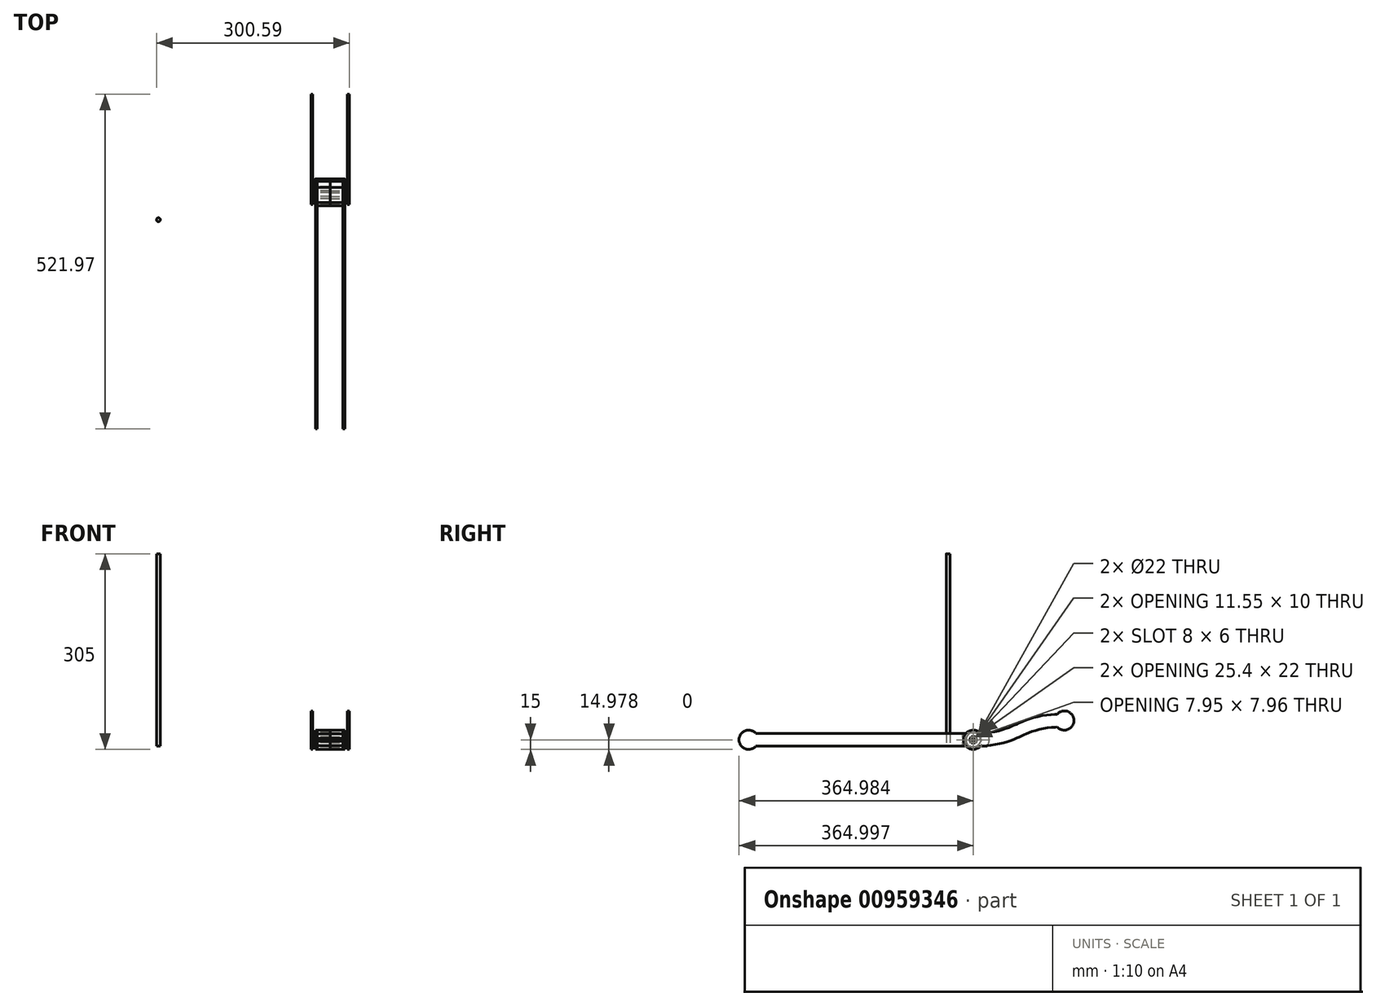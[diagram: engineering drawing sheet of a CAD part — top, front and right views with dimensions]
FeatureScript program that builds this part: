
annotation { "Feature Type Name" : "Feature", "Feature Type Description" : "" }
export const myFeature = defineFeature(function(context is Context, id is Id, definition is map)
    precondition{}
    {
        {
            var Q0;
            Q0=qCreatedBy(makeId("Right.planeOp"),FACE);
            var sketch = newSketch(context, id + "F0", { "sketchPlane" : qUnion([Q0])});
            skLineSegment(sketch, "E0", {"start": v(-170.3, 0) * mm, "end": v(157.34, 0) * mm});
            skLineSegment(sketch, "E1.0", {"start": v(-170.3, 20) * mm, "end": v(157.34, 20) * mm});
            skLineSegment(sketch, "E2.0", {"start": v(-181.48, 10) * mm, "end": v(168.52, 10) * mm, "construction": true});
            skArc(sketch, "E3", {"start": v(157.34, 0) * mm, "mid": v(168.52, -5) * mm, "end": v(179.7, 0) * mm});
            skArc(sketch, "E4", {"start": v(-170.3, 20) * mm, "mid": v(-196.48, 10) * mm, "end": v(-170.3, 0) * mm});
            skPoint(sketch, "E5.end.orphan", {"position": v(-181.48, 0) * mm});
            skLineSegment(sketch, "E6", {"start": v(179.7, 20) * mm, "end": v(189.7, 20) * mm});
            skLineSegment(sketch, "E7", {"start": v(179.7, 0) * mm, "end": v(189.7, 0) * mm});
            skArc(sketch, "E8", {"start": v(189.7, 0) * mm, "mid": v(193.52, 10) * mm, "end": v(189.7, 20) * mm});
            skArc(sketch, "E9.trimOffspring", {"start": v(179.7, 20) * mm, "mid": v(168.52, 25) * mm, "end": v(157.34, 20) * mm});
            skSolve(sketch);
        }
        {
            var Q0;
            Q0=qCreatedBy(makeId("Right.planeOp"),FACE);
            cPlane(context, id + "F1", {"entities" : qUnion([Q0]), "cplaneType" : CPlaneType.OFFSET, "offset" : 20 * mm, "width" : 150 * mm, "height" : 150 * mm});
        }
        {
            var Q0;
            Q0=qCreatedBy(id+"F1.planeOp",FACE);
            var sketch = newSketch(context, id + "F2", { "sketchPlane" : qUnion([Q0])});
            skLineSegment(sketch, "E10.0.0", {"start": v(-170.3, 0) * mm, "end": v(157.34, 0) * mm});
            skLineSegment(sketch, "E10.0.1", {"start": v(157.34, 0) * mm, "end": v(157.34, 0) * mm});
            skLineSegment(sketch, "E10.0.2", {"start": v(157.34, 20) * mm, "end": v(-170.3, 20) * mm});
            skArc(sketch, "E10.0.3", {"start": v(-170.3, 20) * mm, "mid": v(-196.48, 10) * mm, "end": v(-170.3, 0) * mm});
            skPoint(sketch, "E11.0", {"position": v(168.52, 25) * mm});
            skArc(sketch, "E12.0", {"start": v(179.7, 20) * mm, "mid": v(168.52, 25) * mm, "end": v(157.34, 20) * mm});
            skArc(sketch, "E13.0", {"start": v(157.34, 0) * mm, "mid": v(168.52, -5) * mm, "end": v(179.7, 0) * mm});
            skLineSegment(sketch, "E14.0", {"start": v(179.7, 0) * mm, "end": v(189.7, 0) * mm});
            skArc(sketch, "E15.0", {"start": v(189.7, 0) * mm, "mid": v(193.52, 10) * mm, "end": v(189.7, 20) * mm});
            skPoint(sketch, "E16.0", {"position": v(184.7, 20) * mm});
            skLineSegment(sketch, "E17.0", {"start": v(179.7, 20) * mm, "end": v(189.7, 20) * mm});
            skSolve(sketch);
        }
        {
            var Q0;
            Q0=qCreatedBy(makeId("Right.planeOp"),FACE);
            var sketch = newSketch(context, id + "F3", { "sketchPlane" : qUnion([Q0])});
            skArc(sketch, "E18.converted", {"start": v(179.48, 20.24) * mm, "mid": v(153.52, 9.68) * mm, "end": v(179.9, 0.24) * mm});
            skPoint(sketch, "E19.orphan", {"position": v(179.7, 0) * mm});
            skCircle(sketch, "E20", {"center": v(310.5, 40) * mm, "radius": 100 * mm, "construction": true});
            skLineSegment(sketch, "E21", {"start": v(-192.7, -60) * mm, "end": v(245.23, -60) * mm, "construction": true});
            skArc(sketch, "E22", {"start": v(295.5, 40) * mm, "mid": v(295.5, 39.78) * mm, "end": v(295.5, 39.55) * mm});
            skFitSpline(sketch, "E23", {"points": [v(168.52, 10) * mm, v(310.5, 40) * mm], "startDerivative": vector(225, 0) * mm, "endDerivative": vector(225, 0) * mm, "construction": true});
            skLineSegment(sketch, "E24", {"start": v(310.5, 40) * mm, "end": v(235.5, 40) * mm, "construction": true});
            skLineSegment(sketch, "E25", {"start": v(168.52, 10) * mm, "end": v(243.52, 10) * mm, "construction": true});
            skFitSpline(sketch, "E26.0", {"points": [v(168.52, 20) * mm, v(173.04, 20) * mm, v(181.4, 20.23) * mm, v(192.18, 21.14) * mm, v(201.44, 22.54) * mm, v(209.47, 24.32) * mm, v(216.56, 26.42) * mm, v(221.96, 28.38) * mm, v(226.13, 30.06) * mm, v(229.22, 31.37) * mm, v(232.3, 32.73) * mm, v(235.4, 34.12) * mm, v(238.58, 35.54) * mm, v(241.84, 36.98) * mm, v(245.21, 38.41) * mm, v(249.9, 40.3) * mm, v(256.18, 42.59) * mm, v(264.56, 45.06) * mm, v(273.96, 47.15) * mm, v(284.55, 48.74) * mm, v(296.55, 49.76) * mm, v(305.64, 50) * mm, v(310.5, 50) * mm]});
            skFitSpline(sketch, "E27.0", {"points": [v(168.52, 0) * mm, v(173.37, 0) * mm, v(182.46, 0.24) * mm, v(194.46, 1.26) * mm, v(205.05, 2.85) * mm, v(214.45, 4.94) * mm, v(222.83, 7.41) * mm, v(229.1, 9.7) * mm, v(233.8, 11.59) * mm, v(237.18, 13.02) * mm, v(240.43, 14.46) * mm, v(243.6, 15.88) * mm, v(246.71, 17.27) * mm, v(249.8, 18.63) * mm, v(252.88, 19.94) * mm, v(257.05, 21.62) * mm, v(262.45, 23.58) * mm, v(269.54, 25.68) * mm, v(277.57, 27.46) * mm, v(286.83, 28.86) * mm, v(297.6, 29.77) * mm, v(305.97, 30) * mm, v(310.5, 30) * mm]});
            skArc(sketch, "E28.trimOffspring", {"start": v(183.52, 10) * mm, "mid": v(183.52, 10.22) * mm, "end": v(183.51, 10.45) * mm});
            skArc(sketch, "E29.trimOffspring", {"start": v(299.53, 29.76) * mm, "mid": v(325.49, 40.32) * mm, "end": v(299.1, 49.76) * mm});
            skArc(sketch, "E30", {"start": v(310.5, 40) * mm, "mid": v(305.5, 57.9) * mm, "end": v(298.26, 75) * mm, "construction": true});
            skCircle(sketch, "E31", {"center": v(298.26, 75) * mm, "radius": 100 * mm, "construction": true});
            skSolve(sketch);
        }
        {
            var Q0;
            Q0=makeQuery(id+"F2.imprint","IMPRINT",FACE,{"disambiguationData":[TD([[makeQuery(id+"F2.imprint","IMPRINT",EDGE,{"derivedFrom":sQuery(id+"F2.wireOp",EDGE,"E10.0.0")}),1.0]])]});
            extrude(context, id + "F4", {"entities" : qUnion([Q0]), "depth" : 3 * mm, "offsetDistance" : 25 * mm});
        }
        {
            var Q0;
            Q0=makeQuery(id+"F2.imprint","IMPRINT",FACE,{"disambiguationData":[TD([[makeQuery(id+"F2.imprint","IMPRINT",EDGE,{"derivedFrom":sQuery(id+"F2.wireOp",EDGE,"E10.0.0")}),1.0]])]});
            var sketch = newSketch(context, id + "F5", { "sketchPlane" : qUnion([Q0])});
            skPoint(sketch, "E32.0", {"position": v(168.52, 10) * mm});
            skPoint(sketch, "E33.0.midPoint", {"position": v(161.02, 0) * mm});
            skArc(sketch, "E34.cCircle", {"start": v(180.82, 18.58) * mm, "mid": v(168.52, 25) * mm, "end": v(156.22, 18.58) * mm});
            skPoint(sketch, "E34.0.midPoint", {"position": v(181.5, 17.5) * mm});
            skCircle(sketch, "E35.cCircle", {"center": v(168.52, 10) * mm, "radius": 5 * mm, "construction": true});
            skLineSegment(sketch, "E35.0", {"start": v(171.4, 5) * mm, "end": v(165.63, 5) * mm});
            skLineSegment(sketch, "E35.1", {"start": v(165.63, 5) * mm, "end": v(162.74, 10) * mm});
            skLineSegment(sketch, "E35.2", {"start": v(162.74, 10) * mm, "end": v(165.63, 15) * mm});
            skLineSegment(sketch, "E35.3", {"start": v(165.63, 15) * mm, "end": v(171.4, 15) * mm});
            skLineSegment(sketch, "E35.4", {"start": v(171.4, 15) * mm, "end": v(174.3, 10) * mm});
            skLineSegment(sketch, "E35.5", {"start": v(174.3, 10) * mm, "end": v(171.4, 5) * mm});
            skPoint(sketch, "E35.0.midPoint", {"position": v(168.52, 5) * mm});
            skCircle(sketch, "E36.cCircle", {"center": v(168.52, 10) * mm, "radius": 11 * mm});
            skLineSegment(sketch, "E36.0", {"start": v(162.17, 21) * mm, "end": v(174.87, 21) * mm});
            skLineSegment(sketch, "E36.1", {"start": v(174.87, 21) * mm, "end": v(181.22, 10) * mm});
            skLineSegment(sketch, "E36.2", {"start": v(181.22, 10) * mm, "end": v(174.87, -1) * mm});
            skLineSegment(sketch, "E36.3", {"start": v(174.87, -1) * mm, "end": v(162.17, -1) * mm});
            skLineSegment(sketch, "E36.4", {"start": v(162.17, -1) * mm, "end": v(155.82, 10) * mm});
            skLineSegment(sketch, "E36.5", {"start": v(155.82, 10) * mm, "end": v(162.17, 21) * mm});
            skPoint(sketch, "E36.0.midPoint", {"position": v(168.52, 21) * mm});
            skPoint(sketch, "E37.0.midPoint", {"position": v(168.52, 22.71) * mm});
            skArc(sketch, "E38", {"start": v(156.22, 18.58) * mm, "mid": v(151.3, 16.78) * mm, "end": v(153.67, 12.12) * mm});
            skPoint(sketch, "E38.centerSnap0", {"position": v(159, 15.5) * mm});
            skArc(sketch, "E39", {"start": v(153.67, 7.88) * mm, "mid": v(151.3, 3.22) * mm, "end": v(156.22, 1.42) * mm});
            skPoint(sketch, "E39.centerSnap0", {"position": v(159, 4.5) * mm});
            skLineSegment(sketch, "E40", {"start": v(168.52, 10.86) * mm, "end": v(168.52, -9.48) * mm, "construction": true});
            skArc(sketch, "E41.MirrorC", {"start": v(180.82, 18.58) * mm, "mid": v(185.73, 16.78) * mm, "end": v(183.37, 12.12) * mm});
            skArc(sketch, "E42.MirrorC", {"start": v(183.37, 7.88) * mm, "mid": v(185.73, 3.22) * mm, "end": v(180.82, 1.42) * mm});
            skArc(sketch, "E43.trimOffspring", {"start": v(183.37, 7.88) * mm, "mid": v(183.52, 10) * mm, "end": v(183.37, 12.12) * mm});
            skArc(sketch, "E44.trimOffspring", {"start": v(156.22, 1.42) * mm, "mid": v(168.52, -5) * mm, "end": v(180.82, 1.42) * mm});
            skArc(sketch, "E45.trimOffspring", {"start": v(153.67, 12.12) * mm, "mid": v(153.52, 10) * mm, "end": v(153.67, 7.88) * mm});
            skSolve(sketch);
        }
        {
            var Q0;
            Q0=makeQuery(id+"F2.imprint","IMPRINT",FACE,{"disambiguationData":[TD([[makeQuery(id+"F2.imprint","IMPRINT",EDGE,{"derivedFrom":sQuery(id+"F2.wireOp",EDGE,"E10.0.0")}),1.0]])]});
            var sketch = newSketch(context, id + "F6", { "sketchPlane" : qUnion([Q0])});
            skPoint(sketch, "E46.0", {"position": v(168.52, 10) * mm});
            skCircle(sketch, "E47", {"center": v(168.52, 10) * mm, "radius": 11 * mm});
            skSolve(sketch);
        }
        {
            var Q0;
            Q0=makeQuery(id+"F5.imprint","IMPRINT",FACE,{"disambiguationData":[TD([[makeQuery(id+"F5.imprint","IMPRINT",EDGE,{"derivedFrom":sQuery(id+"F5.wireOp",EDGE,"E35.0")}),1.0]])]});
            var Q1;
            Q1=makeQuery(id+"F5.imprint","IMPRINT",FACE,{"disambiguationData":[TD([[makeQuery(id+"F5.imprint","IMPRINT",EDGE,{"derivedFrom":sQuery(id+"F5.wireOp",EDGE,"E35.0")}),-1.0]])]});
            extrude(context, id + "F7", {"entities" : qUnion([Q0, Q1]), "operationType" : NewBodyOperationType.REMOVE, "depth" : 25 * mm, "offsetDistance" : 25 * mm});
        }
        {
            var Q0;
            Q0=makeQuery(id+"F5.imprint","IMPRINT",FACE,{"disambiguationData":[TD([[makeQuery(id+"F5.imprint","IMPRINT",EDGE,{"derivedFrom":sQuery(id+"F5.wireOp",EDGE,"E35.0")}),-1.0]])]});
            extrude(context, id + "F8", {"entities" : qUnion([Q0]), "oppositeDirection" : true, "depth" : 20 * mm, "offsetDistance" : 25 * mm});
        }
        {
            var Q0;
            {var subQ13=sQuery(id+"F5.wireOp",EDGE,"E34.cCircle");var subQ14=makeQuery(id+"F5.imprint","INTERSECT",VERTEX,{"derivedFrom":[makeQuery(id+"F2.imprint","IMPRINT",EDGE,{"derivedFrom":sQuery(id+"F2.wireOp",EDGE,"E10.0.0")}),subQ13]});Q0=makeQuery(id+"F5.imprint","IMPRINT",FACE,{"disambiguationData":[TD([[makeQuery(id+"F5.imprint","IMPRINT",EDGE,{"disambiguationData":[TD([[subQ14,-1.0]])],"derivedFrom":subQ13}),1.0]])]});}
            var Q1;
            {var subQ0=sQuery(id+"F5.wireOp",EDGE,"E41.MirrorC");Q1=makeQuery(id+"F5.imprint","IMPRINT",FACE,{"disambiguationData":[TD([[makeQuery(id+"F5.imprint","IMPRINT",EDGE,{"derivedFrom":subQ0}),-1.0]])]});}
            var Q2;
            {var subQ0=sQuery(id+"F5.wireOp",EDGE,"E42.MirrorC");Q2=makeQuery(id+"F5.imprint","IMPRINT",FACE,{"disambiguationData":[TD([[makeQuery(id+"F5.imprint","IMPRINT",EDGE,{"derivedFrom":subQ0}),-1.0]])]});}
            extrude(context, id + "F9", {"entities" : qUnion([Q0, Q1, Q2]), "oppositeDirection" : true, "depth" : 20 * mm, "offsetDistance" : 25 * mm});
        }
        {
            var Q0;
            Q0=makeQuery(id+"F2.imprint","IMPRINT",FACE,{"disambiguationData":[TD([[makeQuery(id+"F2.imprint","IMPRINT",EDGE,{"derivedFrom":sQuery(id+"F2.wireOp",EDGE,"E10.0.0")}),1.0]])]});
            var sketch = newSketch(context, id + "F10", { "sketchPlane" : qUnion([Q0])});
            skPoint(sketch, "E48.0", {"position": v(168.52, 10) * mm});
            skCircle(sketch, "E49", {"center": v(168.52, 10) * mm, "radius": 4 * mm});
            skSolve(sketch);
        }
        {
            var Q0;
            Q0 = qSketchRegion(id + "F10", true);
            extrude(context, id + "F11", {"entities" : qUnion([Q0]), "operationType" : NewBodyOperationType.ADD, "depth" : 10 * mm, "offsetDistance" : 25 * mm});
        }
        {
            var Q0;
            Q0=makeQuery(id+"F4.opExtrude","CAP_FACE",FACE,{"disambiguationData":[OSD([sQuery(id+"F2.wireOp",EDGE,"E10.0.0"),sQuery(id+"F2.wireOp",EDGE,"E10.0.1"),sQuery(id+"F2.wireOp",EDGE,"E10.0.2"),sQuery(id+"F2.wireOp",EDGE,"E10.0.3")])],"isStart":false});
            var sketch = newSketch(context, id + "F12", { "sketchPlane" : qUnion([Q0])});
            skFitSpline(sketch, "E50.0.0", {"points": [v(299.1, 49.76) * mm, v(298.33, 49.73) * mm, v(293.26, 49.48) * mm, v(284.55, 48.74) * mm, v(273.96, 47.15) * mm, v(264.56, 45.06) * mm, v(256.18, 42.59) * mm, v(249.9, 40.3) * mm, v(245.21, 38.41) * mm, v(241.84, 36.98) * mm, v(238.58, 35.54) * mm, v(235.4, 34.12) * mm, v(232.3, 32.73) * mm, v(229.22, 31.37) * mm, v(226.13, 30.06) * mm, v(221.96, 28.38) * mm, v(216.56, 26.42) * mm, v(209.47, 24.32) * mm, v(201.44, 22.54) * mm, v(192.18, 21.14) * mm, v(184.5, 20.49) * mm, v(180.03, 20.27) * mm, v(179.48, 20.24) * mm]});
            skArc(sketch, "E50.0.1", {"start": v(179.48, 20.24) * mm, "mid": v(153.52, 9.68) * mm, "end": v(179.9, 0.24) * mm});
            skFitSpline(sketch, "E50.0.2", {"points": [v(179.9, 0.24) * mm, v(180.68, 0.27) * mm, v(185.75, 0.52) * mm, v(194.46, 1.26) * mm, v(205.05, 2.85) * mm, v(214.45, 4.94) * mm, v(222.83, 7.41) * mm, v(229.1, 9.7) * mm, v(233.8, 11.59) * mm, v(237.18, 13.02) * mm, v(240.43, 14.46) * mm, v(243.6, 15.88) * mm, v(246.71, 17.27) * mm, v(249.8, 18.63) * mm, v(252.88, 19.94) * mm, v(257.05, 21.62) * mm, v(262.45, 23.58) * mm, v(269.54, 25.68) * mm, v(277.57, 27.46) * mm, v(286.83, 28.86) * mm, v(294.51, 29.51) * mm, v(298.98, 29.73) * mm, v(299.53, 29.76) * mm]});
            skArc(sketch, "E50.0.3", {"start": v(299.53, 29.76) * mm, "mid": v(325.49, 40.32) * mm, "end": v(299.1, 49.76) * mm});
            skLineSegment(sketch, "E51.0", {"start": v(171.4, 15) * mm, "end": v(174.3, 10) * mm});
            skLineSegment(sketch, "E52.0", {"start": v(174.3, 10) * mm, "end": v(171.4, 5) * mm});
            skLineSegment(sketch, "E53.0", {"start": v(165.63, 15) * mm, "end": v(171.4, 15) * mm});
            skLineSegment(sketch, "E54.0", {"start": v(162.74, 10) * mm, "end": v(165.63, 15) * mm});
            skLineSegment(sketch, "E55.0", {"start": v(165.63, 5) * mm, "end": v(162.74, 10) * mm});
            skLineSegment(sketch, "E56.0", {"start": v(171.4, 5) * mm, "end": v(165.63, 5) * mm});
            skSolve(sketch);
        }
        {
            var Q0;
            {var subQ0=sQuery(id+"F12.wireOp",EDGE,"E50.0.0");Q0=makeQuery(id+"F12.imprint","IMPRINT",FACE,{"disambiguationData":[TD([[makeQuery(id+"F12.imprint","IMPRINT",EDGE,{"derivedFrom":subQ0}),1.0]])]});}
            var Q1;
            Q1=makeQuery(id+"F12.imprint","IMPRINT",FACE,{"disambiguationData":[TD([[makeQuery(id+"F12.imprint","IMPRINT",EDGE,{"derivedFrom":sQuery(id+"F12.wireOp",EDGE,"1fd20273-663b-4c58-b14a-399989266dd2.0")}),1.0]])]});
            var Q2;
            {var subQ0=sQuery(id+"F12.wireOp",EDGE,"E50.0.1");var subQ1=sQuery(id+"F2.wireOp",EDGE,"E10.0.0");var subQ2=makeQuery(id+"F12.imprint","INTERSECT",VERTEX,{"derivedFrom":[makeQuery(id+"F4.opExtrude","CAP_EDGE",EDGE,{"disambiguationData":[OSD([subQ1])],"isStart":false}),subQ0]});Q2=makeQuery(id+"F12.imprint","IMPRINT",FACE,{"disambiguationData":[TD([[makeQuery(id+"F12.imprint","IMPRINT",EDGE,{"disambiguationData":[TD([[subQ2,1.0]])],"derivedFrom":subQ0}),1.0]])]});}
            var Q3;
            Q3=makeQuery(id+"F12.imprint","IMPRINT",FACE,{"disambiguationData":[TD([[makeQuery(id+"F12.imprint","IMPRINT",EDGE,{"derivedFrom":sQuery(id+"F12.wireOp",EDGE,"E51.0")}),1.0]])]});
            extrude(context, id + "F13", {"entities" : qUnion([Q0, Q1, Q2, Q3]), "depth" : 3 * mm, "offsetDistance" : 25 * mm});
        }
        {
            var Q0;
            Q0=makeQuery(id+"F11.opExtrude","CAP_FACE",FACE,{"disambiguationData":[OSD([sQuery(id+"F10.wireOp",EDGE,"E49")])],"isStart":false});
            var sketch = newSketch(context, id + "F14", { "sketchPlane" : qUnion([Q0])});
            skArc(sketch, "E57.0", {"start": v(165.52, 12.65) * mm, "mid": v(164.52, 10) * mm, "end": v(165.52, 7.35) * mm});
            skLineSegment(sketch, "E58", {"start": v(165.52, 12.65) * mm, "end": v(165.52, 7.35) * mm});
            skLineSegment(sketch, "E59", {"start": v(171.52, 12.65) * mm, "end": v(171.52, 7.35) * mm});
            skArc(sketch, "E60.trimOffspring", {"start": v(171.52, 7.35) * mm, "mid": v(172.52, 10) * mm, "end": v(171.52, 12.65) * mm});
            skSolve(sketch);
        }
        {
            var Q0;
            Q0=makeQuery(id+"F14.imprint","IMPRINT",FACE,{"disambiguationData":[TD([[makeQuery(id+"F14.imprint","IMPRINT",EDGE,{"derivedFrom":sQuery(id+"F14.wireOp",EDGE,"E57.0")}),1.0]])]});
            var Q1;
            Q1=makeQuery(id+"F14.imprint","IMPRINT",FACE,{"disambiguationData":[TD([[makeQuery(id+"F14.imprint","IMPRINT",EDGE,{"derivedFrom":sQuery(id+"F14.wireOp",EDGE,"E59")}),1.0]])]});
            extrude(context, id + "F15", {"entities" : qUnion([Q0, Q1]), "operationType" : NewBodyOperationType.REMOVE, "oppositeDirection" : true, "depth" : 5 * mm, "offsetDistance" : 25 * mm});
        }
        {
            var Q0;
            Q0=makeQuery(id+"F11.opExtrude","CAP_FACE",FACE,{"disambiguationData":[OSD([sQuery(id+"F10.wireOp",EDGE,"E49")])],"isStart":false});
            var sketch = newSketch(context, id + "F16", { "sketchPlane" : qUnion([Q0])});
            skArc(sketch, "E61.0", {"start": v(171.52, 12.65) * mm, "mid": v(168.52, 14) * mm, "end": v(165.52, 12.65) * mm});
            skArc(sketch, "E62.0", {"start": v(165.52, 7.35) * mm, "mid": v(168.52, 6) * mm, "end": v(171.52, 7.35) * mm});
            skLineSegment(sketch, "E63.0", {"start": v(171.52, 12.65) * mm, "end": v(171.52, 7.35) * mm});
            skLineSegment(sketch, "E64.0", {"start": v(165.52, 12.65) * mm, "end": v(165.52, 7.35) * mm});
            skLineSegment(sketch, "E65.0.0", {"start": v(165.63, 5) * mm, "end": v(171.4, 5) * mm});
            skLineSegment(sketch, "E65.0.1", {"start": v(171.4, 5) * mm, "end": v(174.3, 10) * mm});
            skLineSegment(sketch, "E65.0.2", {"start": v(174.3, 10) * mm, "end": v(171.4, 15) * mm});
            skLineSegment(sketch, "E65.0.3", {"start": v(171.4, 15) * mm, "end": v(165.63, 15) * mm});
            skLineSegment(sketch, "E65.0.4", {"start": v(165.63, 15) * mm, "end": v(162.74, 10) * mm});
            skLineSegment(sketch, "E65.0.5", {"start": v(162.74, 10) * mm, "end": v(165.63, 5) * mm});
            skSolve(sketch);
        }
        {
            var Q0;
            Q0=makeQuery(id+"F16.imprint","IMPRINT",FACE,{"disambiguationData":[TD([[makeQuery(id+"F16.imprint","IMPRINT",EDGE,{"derivedFrom":sQuery(id+"F16.wireOp",EDGE,"E61.0")}),-1.0]])]});
            extrude(context, id + "F17", {"entities" : qUnion([Q0]), "oppositeDirection" : true, "depth" : 5 * mm, "offsetDistance" : 25 * mm});
        }
        {
            var Q0;
            Q0=makeQuery(id+"F13.opExtrude","SWEPT_BODY",BODY,{"disambiguationData":[OSD([sQuery(id+"F2.wireOp",EDGE,"E10.0.0"),sQuery(id+"F2.wireOp",EDGE,"E10.0.1"),sQuery(id+"F2.wireOp",EDGE,"E10.0.2"),sQuery(id+"F2.wireOp",EDGE,"E10.0.3"),sQuery(id+"F5.wireOp",EDGE,"E36.cCircle"),sQuery(id+"F12.wireOp",EDGE,"E50.0.0"),sQuery(id+"F12.wireOp",EDGE,"E50.0.1"),sQuery(id+"F12.wireOp",EDGE,"E50.0.2"),sQuery(id+"F12.wireOp",EDGE,"E50.0.3")])]});
            var Q1;
            Q1=makeQuery(id+"F4.opExtrude","CAP_FACE",FACE,{"disambiguationData":[OSD([sQuery(id+"F2.wireOp",EDGE,"E10.0.0"),sQuery(id+"F2.wireOp",EDGE,"E10.0.1"),sQuery(id+"F2.wireOp",EDGE,"E10.0.2"),sQuery(id+"F2.wireOp",EDGE,"E10.0.3")])],"isStart":false});
            transform(context, id + "F18", {"entities" : qUnion([Q0]), "transformType" : TransformType.TRANSLATION_DISTANCE, "transformDirection" : qUnion([Q1]), "distance" : 4 * mm, "makeCopy" : false});
        }
        {
            var Q0;
            Q0=makeQuery(id+"F4.opExtrude","SWEPT_BODY",BODY,{"disambiguationData":[OSD([sQuery(id+"F2.wireOp",EDGE,"E10.0.0"),sQuery(id+"F2.wireOp",EDGE,"E10.0.1"),sQuery(id+"F2.wireOp",EDGE,"E10.0.2"),sQuery(id+"F2.wireOp",EDGE,"E10.0.3")])]});
            var Q1;
            Q1=makeQuery(id+"F8.opExtrude","SWEPT_BODY",BODY,{"disambiguationData":[OSD([sQuery(id+"F5.wireOp",EDGE,"E35.0"),sQuery(id+"F5.wireOp",EDGE,"E35.1"),sQuery(id+"F5.wireOp",EDGE,"E35.2"),sQuery(id+"F5.wireOp",EDGE,"E35.3"),sQuery(id+"F5.wireOp",EDGE,"E35.4"),sQuery(id+"F5.wireOp",EDGE,"E35.5")])]});
            var Q2;
            Q2=makeQuery(id+"F9.opExtrude","SWEPT_BODY",BODY,{"disambiguationData":[OSD([sQuery(id+"F5.wireOp",EDGE,"E34.cCircle"),sQuery(id+"F5.wireOp",EDGE,"E36.0"),sQuery(id+"F5.wireOp",EDGE,"E36.1"),sQuery(id+"F5.wireOp",EDGE,"E36.2"),sQuery(id+"F5.wireOp",EDGE,"E36.3"),sQuery(id+"F5.wireOp",EDGE,"E36.4"),sQuery(id+"F5.wireOp",EDGE,"E36.5"),sQuery(id+"F5.wireOp",EDGE,"E38"),sQuery(id+"F5.wireOp",EDGE,"E39"),sQuery(id+"F5.wireOp",EDGE,"E41.MirrorC"),sQuery(id+"F5.wireOp",EDGE,"E42.MirrorC"),sQuery(id+"F5.wireOp",EDGE,"E43.trimOffspring"),sQuery(id+"F5.wireOp",EDGE,"E44.trimOffspring"),sQuery(id+"F5.wireOp",EDGE,"E45.trimOffspring")])]});
            var Q3;
            Q3=makeQuery(id+"F13.opExtrude","SWEPT_BODY",BODY,{"disambiguationData":[OSD([sQuery(id+"F12.wireOp",EDGE,"E50.0.0"),sQuery(id+"F12.wireOp",EDGE,"E50.0.1"),sQuery(id+"F12.wireOp",EDGE,"E50.0.2"),sQuery(id+"F12.wireOp",EDGE,"E50.0.3"),sQuery(id+"F12.wireOp",EDGE,"E51.0"),sQuery(id+"F12.wireOp",EDGE,"E52.0"),sQuery(id+"F12.wireOp",EDGE,"E53.0"),sQuery(id+"F12.wireOp",EDGE,"E54.0"),sQuery(id+"F12.wireOp",EDGE,"E55.0"),sQuery(id+"F12.wireOp",EDGE,"E56.0")])]});
            var Q4;
            Q4=makeQuery(id+"F17.opExtrude","SWEPT_BODY",BODY,{"disambiguationData":[OSD([sQuery(id+"F16.wireOp",EDGE,"E61.0"),sQuery(id+"F16.wireOp",EDGE,"E62.0"),sQuery(id+"F16.wireOp",EDGE,"E63.0"),sQuery(id+"F16.wireOp",EDGE,"E64.0"),sQuery(id+"F16.wireOp",EDGE,"E65.0.0"),sQuery(id+"F16.wireOp",EDGE,"E65.0.1"),sQuery(id+"F16.wireOp",EDGE,"E65.0.2"),sQuery(id+"F16.wireOp",EDGE,"E65.0.3"),sQuery(id+"F16.wireOp",EDGE,"E65.0.4"),sQuery(id+"F16.wireOp",EDGE,"E65.0.5")])]});
            var Q5;
            Q5=qCreatedBy(makeId("Right.planeOp"),FACE);
            mirror(context, id + "F19", {"entities" : qUnion([Q0, Q1, Q2, Q3, Q4]), "mirrorPlane" : qUnion([Q5])});
        }
        {
            var Q0;
            Q0=qCreatedBy(makeId("Top.planeOp"),FACE);
            var sketch = newSketch(context, id + "F20", { "sketchPlane" : qUnion([Q0])});
            skCircle(sketch, "E66", {"center": v(-267.6, 129.62) * mm, "radius": 3 * mm});
            skSolve(sketch);
        }
        {
            var Q0;
            Q0=makeQuery(id+"F20.imprint","IMPRINT",FACE,{"disambiguationData":[TD([[makeQuery(id+"F20.imprint","IMPRINT",EDGE,{"derivedFrom":sQuery(id+"F20.wireOp",EDGE,"E66")}),1.0]])]});
            extrude(context, id + "F21", {"entities" : qUnion([Q0]), "depth" : 300 * mm, "offsetDistance" : 25 * mm});
        }
    });
